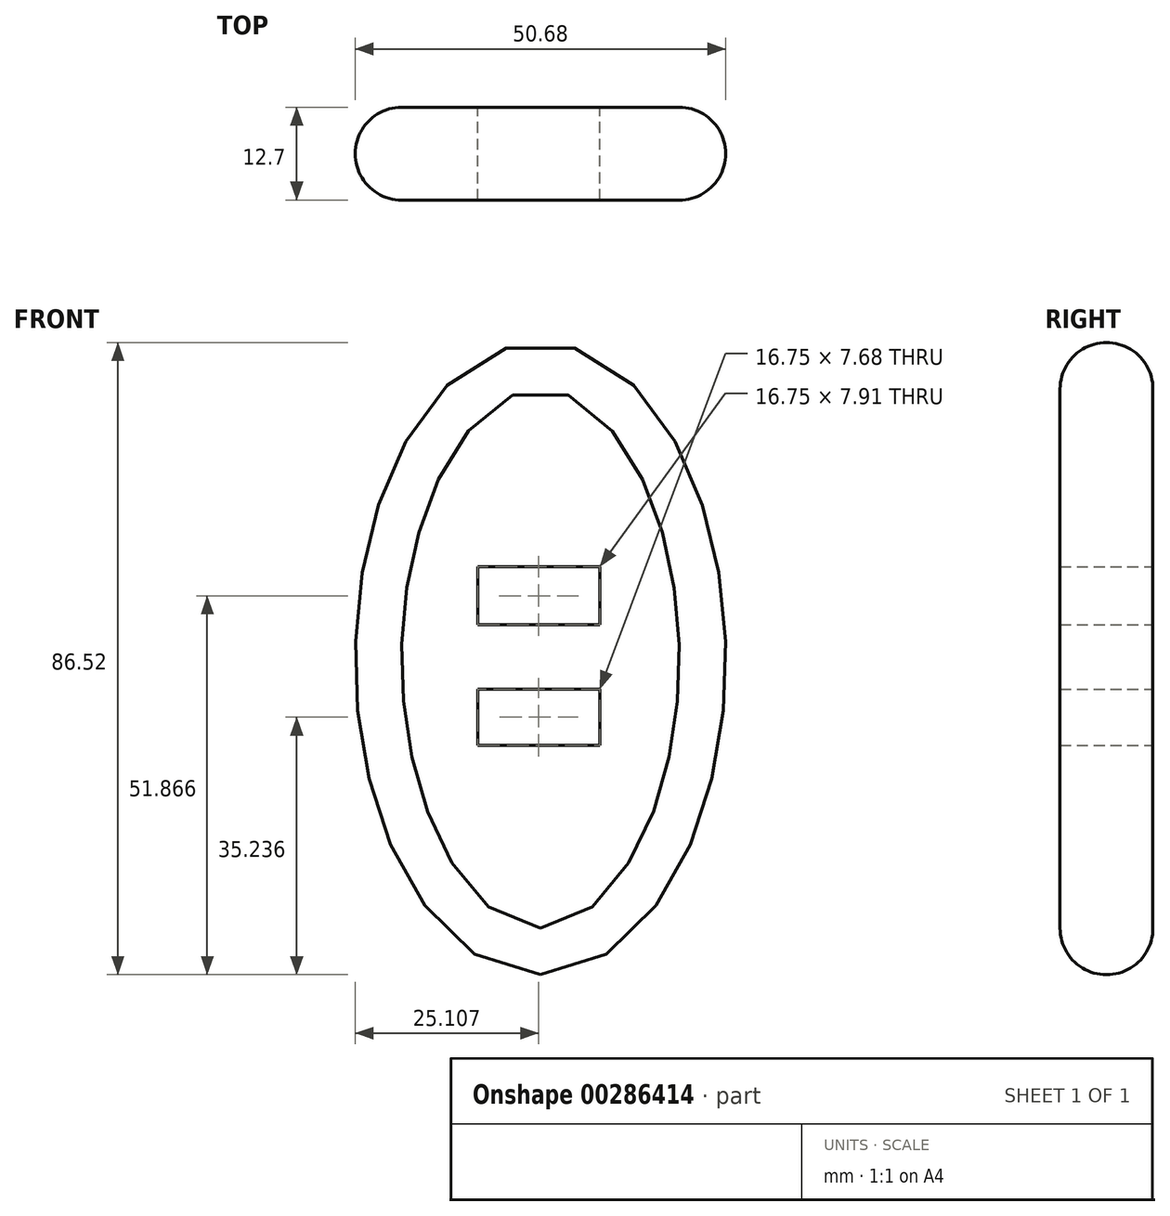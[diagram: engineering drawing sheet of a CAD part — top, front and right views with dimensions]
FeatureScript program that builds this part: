
annotation { "Feature Type Name" : "Feature", "Feature Type Description" : "" }
export const myFeature = defineFeature(function(context is Context, id is Id, definition is map)
    precondition{}
    {
        {
            var Q0;
            Q0=qCreatedBy(makeId("Front.planeOp"),FACE);
            var sketch = newSketch(context, id + "F0", { "sketchPlane" : qUnion([Q0])});
            skEllipse(sketch, "E0", {"center": v(0, 0) * mm, "majorRadius": 43.26 * mm, "minorRadius": 25.34 * mm, "majorAxis": v(0, -1)});
            skSolve(sketch);
        }
        {
            var Q0;
            Q0 = qSketchRegion(id + "F0", true);
            extrude(context, id + "F1", {"entities" : qUnion([Q0]), "depth" : 12.7 * mm});
        }
        {
            var Q0;
            Q0=makeQuery(id+"F1.opExtrude","CAP_EDGE",EDGE,{"disambiguationData":[OSD([sQuery(id+"F0.wireOp",EDGE,"E0")])],"isStart":true});
            fillet(context, id + "F2", {"entities" : qUnion([Q0]), "radius" : 6.35 * mm, "tangentPropagation" : true, "allowEdgeOverflow" : false});
        }
        {
            var Q0;
            Q0=makeQuery(id+"F1.opExtrude","CAP_EDGE",EDGE,{"disambiguationData":[OSD([sQuery(id+"F0.wireOp",EDGE,"E0")])],"isStart":false});
            fillet(context, id + "F3", {"entities" : qUnion([Q0]), "radius" : 6.35 * mm, "tangentPropagation" : true, "allowEdgeOverflow" : false});
        }
        {
            var Q0;
            Q0=makeQuery(id+"F1.opExtrude","CAP_FACE",FACE,{"disambiguationData":[OSD([sQuery(id+"F0.wireOp",EDGE,"E0")])],"isStart":true});
            var sketch = newSketch(context, id + "F4", { "sketchPlane" : qUnion([Q0])});
            skLineSegment(sketch, "E1.bottom", {"start": v(-8.14, 12.56) * mm, "end": v(8.6, 12.56) * mm});
            skLineSegment(sketch, "E1.top", {"start": v(-8.14, 4.65) * mm, "end": v(8.6, 4.65) * mm});
            skLineSegment(sketch, "E1.left", {"start": v(-8.14, 12.56) * mm, "end": v(-8.14, 4.65) * mm});
            skLineSegment(sketch, "E1.right", {"start": v(8.6, 12.56) * mm, "end": v(8.6, 4.65) * mm});
            skLineSegment(sketch, "E2.bottom", {"start": v(-8.14, -4.19) * mm, "end": v(8.6, -4.19) * mm});
            skLineSegment(sketch, "E2.top", {"start": v(-8.14, -11.86) * mm, "end": v(8.6, -11.86) * mm});
            skLineSegment(sketch, "E2.left", {"start": v(-8.14, -4.19) * mm, "end": v(-8.14, -11.86) * mm});
            skLineSegment(sketch, "E2.right", {"start": v(8.6, -4.19) * mm, "end": v(8.6, -11.86) * mm});
            skSolve(sketch);
        }
        {
            var Q0;
            Q0=makeQuery(id+"F4.imprint","IMPRINT",FACE,{"disambiguationData":[TD([[makeQuery(id+"F4.imprint","IMPRINT",EDGE,{"derivedFrom":sQuery(id+"F4.wireOp",EDGE,"E1.bottom")}),-1.0]])]});
            var Q1;
            Q1=makeQuery(id+"F4.imprint","IMPRINT",FACE,{"disambiguationData":[TD([[makeQuery(id+"F4.imprint","IMPRINT",EDGE,{"derivedFrom":sQuery(id+"F4.wireOp",EDGE,"E2.bottom")}),-1.0]])]});
            extrude(context, id + "F5", {"entities" : qUnion([Q0, Q1]), "operationType" : NewBodyOperationType.REMOVE, "oppositeDirection" : true, "depth" : 25.4 * mm});
        }
    });
